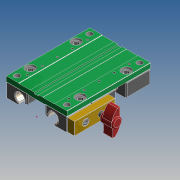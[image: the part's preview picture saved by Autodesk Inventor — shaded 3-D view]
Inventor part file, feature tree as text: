
AUTODESK INVENTOR PART (.ipt)
format: ipt  version: 2015 SP1 (Build 190203100, 203)  size: 6,983,680 bytes
history: native  units: mm
features: other x3, sketch x2, surface_op x1, hole x1, pattern_linear x1, extrude x1
ambient origin geometry x8: Origin, YZ Plane, XZ Plane, XY Plane, X Axis, Y Axis, Z Axis, Center Point
bodies: Solid1 (feature_tree)
feature tree (9):
  other  "WW_10_40_10_HKA_11"
  sketch  "Sketch2"  dims[d0=25.0mm d1=14.0mm d2=50.0mm]
  surface_op  "Stitch Surface1"
  hole  "Hole1"  [1 undecoded]
  pattern_linear  "Rectangular Pattern1"  Count1=5  [1 undecoded]
  extrude  "Extrusion1"  Depth=50.0mm
  sketch  "Sketch3"  dims[d6=2.459mm d7=6.0mm d8=4.0mm d9=2.0mm d10=90.0deg d11=8.8mm d12=20.594885mm d13=50.0mm d15=18.0mm d16=20.0mm d18=50.0mm d19=5.0mm d20=1.5mm d21=10.0mm d22=0.0mm]
  other  "Composite1"
  other  "Srf1"
note: 2 required parameter values undecoded (feature->parameter linkage not recoverable at this tier; creation-order binding heuristic only, values carry confidence <= 0.55)
